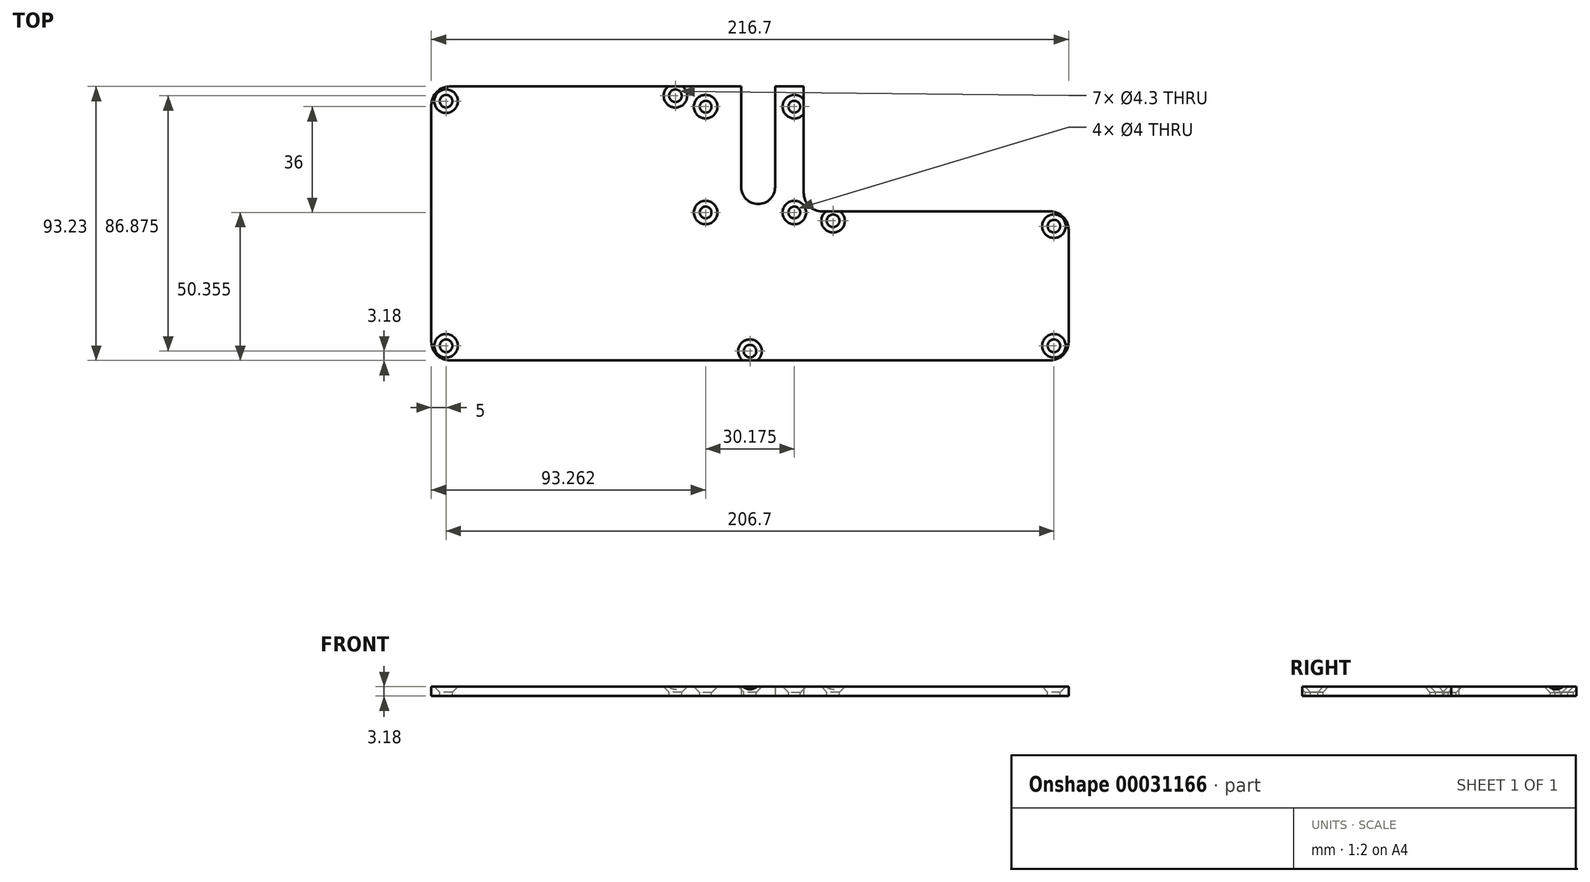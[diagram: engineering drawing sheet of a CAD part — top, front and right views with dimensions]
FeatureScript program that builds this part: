
annotation { "Feature Type Name" : "Feature", "Feature Type Description" : "" }
export const myFeature = defineFeature(function(context is Context, id is Id, definition is map)
    precondition{}
    {
        {
            var Q0;
            Q0=qCreatedBy(makeId("Top.planeOp"),FACE);
            var sketch = newSketch(context, id + "F0", { "sketchPlane" : qUnion([Q0])});
            skLineSegment(sketch, "E0", {"start": v(0, 0) * mm, "end": v(105.38, 0) * mm});
            skLineSegment(sketch, "E1", {"start": v(105.38, 0) * mm, "end": v(105.38, -34.25) * mm});
            skLineSegment(sketch, "E2", {"start": v(116.87, -34.25) * mm, "end": v(116.87, 0) * mm});
            skLineSegment(sketch, "E3", {"start": v(116.87, 0) * mm, "end": v(126.61, 0) * mm});
            skLineSegment(sketch, "E4", {"start": v(126.61, 0) * mm, "end": v(126.61, -42.52) * mm});
            skLineSegment(sketch, "E5", {"start": v(126.61, -42.52) * mm, "end": v(216.7, -42.52) * mm});
            skLineSegment(sketch, "E6", {"start": v(216.7, -42.52) * mm, "end": v(216.7, -93.22) * mm});
            skLineSegment(sketch, "E7", {"start": v(216.7, -93.22) * mm, "end": v(0, -93.23) * mm});
            skLineSegment(sketch, "E8", {"start": v(0, -93.23) * mm, "end": v(0, 0) * mm});
            skArc(sketch, "E9", {"start": v(105.38, -34.25) * mm, "mid": v(111.12, -40) * mm, "end": v(116.87, -34.25) * mm});
            skSolve(sketch);
        }
        {
            var Q0;
            Q0 = qSketchRegion(id + "F0", true);
            extrude(context, id + "F1", {"entities" : qUnion([Q0]), "depth" : 3.17 * mm});
        }
        {
            var Q0;
            Q0=makeQuery(id+"F1.opExtrude","SWEPT_EDGE",EDGE,{"disambiguationData":[OSD([sQuery(id+"F0.wireOp",EDGE,"E0"),sQuery(id+"F0.wireOp",EDGE,"E8")])]});
            var Q1;
            Q1=makeQuery(id+"F1.opExtrude","SWEPT_EDGE",EDGE,{"disambiguationData":[OSD([sQuery(id+"F0.wireOp",EDGE,"E7"),sQuery(id+"F0.wireOp",EDGE,"E8")])]});
            var Q2;
            Q2=makeQuery(id+"F1.opExtrude","SWEPT_EDGE",EDGE,{"disambiguationData":[OSD([sQuery(id+"F0.wireOp",EDGE,"E4"),sQuery(id+"F0.wireOp",EDGE,"E5")])]});
            var Q3;
            Q3=makeQuery(id+"F1.opExtrude","SWEPT_EDGE",EDGE,{"disambiguationData":[OSD([sQuery(id+"F0.wireOp",EDGE,"E5"),sQuery(id+"F0.wireOp",EDGE,"E6")])]});
            var Q4;
            Q4=makeQuery(id+"F1.opExtrude","SWEPT_EDGE",EDGE,{"disambiguationData":[OSD([sQuery(id+"F0.wireOp",EDGE,"E6"),sQuery(id+"F0.wireOp",EDGE,"E7")])]});
            fillet(context, id + "F2", {"entities" : qUnion([Q0, Q1, Q2, Q3, Q4]), "radius" : 6.35 * mm, "tangentPropagation" : true, "allowEdgeOverflow" : false});
        }
        {
            var Q0;
            Q0=makeQuery(id+"F1.opExtrude","CAP_FACE",FACE,{"disambiguationData":[OSD([sQuery(id+"F0.wireOp",EDGE,"E0"),sQuery(id+"F0.wireOp",EDGE,"E1"),sQuery(id+"F0.wireOp",EDGE,"E2"),sQuery(id+"F0.wireOp",EDGE,"E3"),sQuery(id+"F0.wireOp",EDGE,"E4"),sQuery(id+"F0.wireOp",EDGE,"E5"),sQuery(id+"F0.wireOp",EDGE,"E6"),sQuery(id+"F0.wireOp",EDGE,"E7"),sQuery(id+"F0.wireOp",EDGE,"E8"),sQuery(id+"F0.wireOp",EDGE,"E9")])],"isStart":false});
            var sketch = newSketch(context, id + "F3", { "sketchPlane" : qUnion([Q0])});
            skPoint(sketch, "E10", {"position": v(5, -5) * mm});
            skPoint(sketch, "E11", {"position": v(5, -88.22) * mm});
            skPoint(sketch, "E12", {"position": v(211.7, -88.22) * mm});
            skPoint(sketch, "E13", {"position": v(211.7, -47.52) * mm});
            skPoint(sketch, "E14", {"position": v(136.61, -45.7) * mm});
            skPoint(sketch, "E15", {"position": v(83, -3.17) * mm});
            skPoint(sketch, "E16", {"position": v(102.76, -10.83) * mm});
            skPoint(sketch, "E17", {"position": v(121.07, -10.83) * mm});
            skPoint(sketch, "E18", {"position": v(108.35, -90.05) * mm});
            skLineSegment(sketch, "E19", {"start": v(5, -88.22) * mm, "end": v(108.35, -90.05) * mm, "construction": true});
            skLineSegment(sketch, "E20", {"start": v(108.35, -90.05) * mm, "end": v(211.7, -88.22) * mm, "construction": true});
            skSolve(sketch);
        }
        {
            var Q0;
            Q0=sQuery(id+"F3.wireOp",VERTEX,"E10");
            var Q1;
            Q1=sQuery(id+"F3.wireOp",VERTEX,"E11");
            var Q2;
            Q2=sQuery(id+"F3.wireOp",VERTEX,"E12");
            var Q3;
            Q3=sQuery(id+"F3.wireOp",VERTEX,"E13");
            var Q4;
            Q4=sQuery(id+"F3.wireOp",VERTEX,"E14");
            var Q5;
            Q5=sQuery(id+"F3.wireOp",VERTEX,"E15");
            var Q6;
            Q6=sQuery(id+"F3.wireOp",VERTEX,"E18");
            var Q7;
            Q7=makeQuery(id+"F1.opExtrude","SWEPT_BODY",BODY,{"disambiguationData":[OSD([sQuery(id+"F0.wireOp",EDGE,"E0"),sQuery(id+"F0.wireOp",EDGE,"E1"),sQuery(id+"F0.wireOp",EDGE,"E2"),sQuery(id+"F0.wireOp",EDGE,"E3"),sQuery(id+"F0.wireOp",EDGE,"E4"),sQuery(id+"F0.wireOp",EDGE,"E5"),sQuery(id+"F0.wireOp",EDGE,"E6"),sQuery(id+"F0.wireOp",EDGE,"E7"),sQuery(id+"F0.wireOp",EDGE,"E8"),sQuery(id+"F0.wireOp",EDGE,"E9")])]});
            hole(context, id + "F4", {"style" : HoleStyle.C_SINK, "holeDiameter" : 4.3 * mm, "cSinkDiameter" : 8 * mm, "endStyle" : HoleEndStyle.THROUGH, "locations" : qUnion([Q0, Q1, Q2, Q3, Q4, Q5, Q6]), "scope" : qUnion([Q7]), "cSinkAngle" : 90 * degree});
        }
        {
            var Q0;
            Q0=makeQuery(id+"F1.opExtrude","CAP_FACE",FACE,{"disambiguationData":[OSD([sQuery(id+"F0.wireOp",EDGE,"E0"),sQuery(id+"F0.wireOp",EDGE,"E1"),sQuery(id+"F0.wireOp",EDGE,"E2"),sQuery(id+"F0.wireOp",EDGE,"E3"),sQuery(id+"F0.wireOp",EDGE,"E4"),sQuery(id+"F0.wireOp",EDGE,"E5"),sQuery(id+"F0.wireOp",EDGE,"E6"),sQuery(id+"F0.wireOp",EDGE,"E7"),sQuery(id+"F0.wireOp",EDGE,"E8"),sQuery(id+"F0.wireOp",EDGE,"E9")])],"isStart":false});
            var sketch = newSketch(context, id + "F5", { "sketchPlane" : qUnion([Q0])});
            skLineSegment(sketch, "E21", {"start": v(123.44, 0) * mm, "end": v(123.44, -48.88) * mm, "construction": true});
            skLineSegment(sketch, "E22", {"start": v(93.26, 0) * mm, "end": v(93.26, -48.88) * mm, "construction": true});
            skPoint(sketch, "E23", {"position": v(123.44, -42.88) * mm});
            skPoint(sketch, "E24", {"position": v(123.44, -6.88) * mm});
            skPoint(sketch, "E25", {"position": v(93.26, -42.88) * mm});
            skPoint(sketch, "E26", {"position": v(93.26, -6.88) * mm});
            skSolve(sketch);
        }
        {
            var Q0;
            Q0=sQuery(id+"F5.wireOp",VERTEX,"E23");
            var Q1;
            Q1=sQuery(id+"F5.wireOp",VERTEX,"E24");
            var Q2;
            Q2=sQuery(id+"F5.wireOp",VERTEX,"E26");
            var Q3;
            Q3=sQuery(id+"F5.wireOp",VERTEX,"E25");
            var Q4;
            Q4=makeQuery(id+"F1.opExtrude","SWEPT_BODY",BODY,{"disambiguationData":[OSD([sQuery(id+"F0.wireOp",EDGE,"E0"),sQuery(id+"F0.wireOp",EDGE,"E1"),sQuery(id+"F0.wireOp",EDGE,"E2"),sQuery(id+"F0.wireOp",EDGE,"E3"),sQuery(id+"F0.wireOp",EDGE,"E4"),sQuery(id+"F0.wireOp",EDGE,"E5"),sQuery(id+"F0.wireOp",EDGE,"E6"),sQuery(id+"F0.wireOp",EDGE,"E7"),sQuery(id+"F0.wireOp",EDGE,"E8"),sQuery(id+"F0.wireOp",EDGE,"E9")])]});
            hole(context, id + "F6", {"style" : HoleStyle.C_SINK, "holeDiameter" : 4 * mm, "cSinkDiameter" : 8 * mm, "endStyle" : HoleEndStyle.THROUGH, "locations" : qUnion([Q0, Q1, Q2, Q3]), "scope" : qUnion([Q4]), "cSinkAngle" : 90 * degree});
        }
    });
